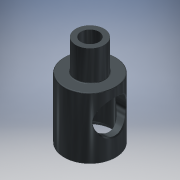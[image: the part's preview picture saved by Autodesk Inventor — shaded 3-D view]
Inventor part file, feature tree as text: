
AUTODESK INVENTOR PART (.ipt)
format: ipt  version: 2018 (Build 220112000, 112)  size: 215,040 bytes
history: native  units: mm
features: sketch x2, revolve x1, extrude x1, chamfer x1
ambient origin geometry x8: Origin, YZ Plane, XZ Plane, XY Plane, X Axis, Y Axis, Z Axis, Center Point
bodies: Solid1 (feature_tree)
feature tree (5):
  revolve  "Revolution1"  [1 undecoded]
  extrude  "Extrusion1"  TaperAngle=45.0deg  [1 undecoded]
  chamfer  "Chamfer1"  Distance=0.74mm
  sketch  "Sketch1"  dims[d0=13.05mm d1=6.4mm]
  sketch  "Sketch2"  dims[d2=11.05mm d3=45.0deg d4=0.74mm d5=1.9mm d6=3.0mm d7=4.0mm d8=5.5mm d9=0.2mm d10=0.2mm d11=0.5mm d12=0.22mm d13=90.0deg d14=7.0mm d15=7.55mm d16=10.0mm d17=0.0mm d18=0.2mm d19=2.0mm d20=45.0deg d21=0.2mm]
note: 2 required parameter values undecoded (feature->parameter linkage not recoverable at this tier; creation-order binding heuristic only, values carry confidence <= 0.55)